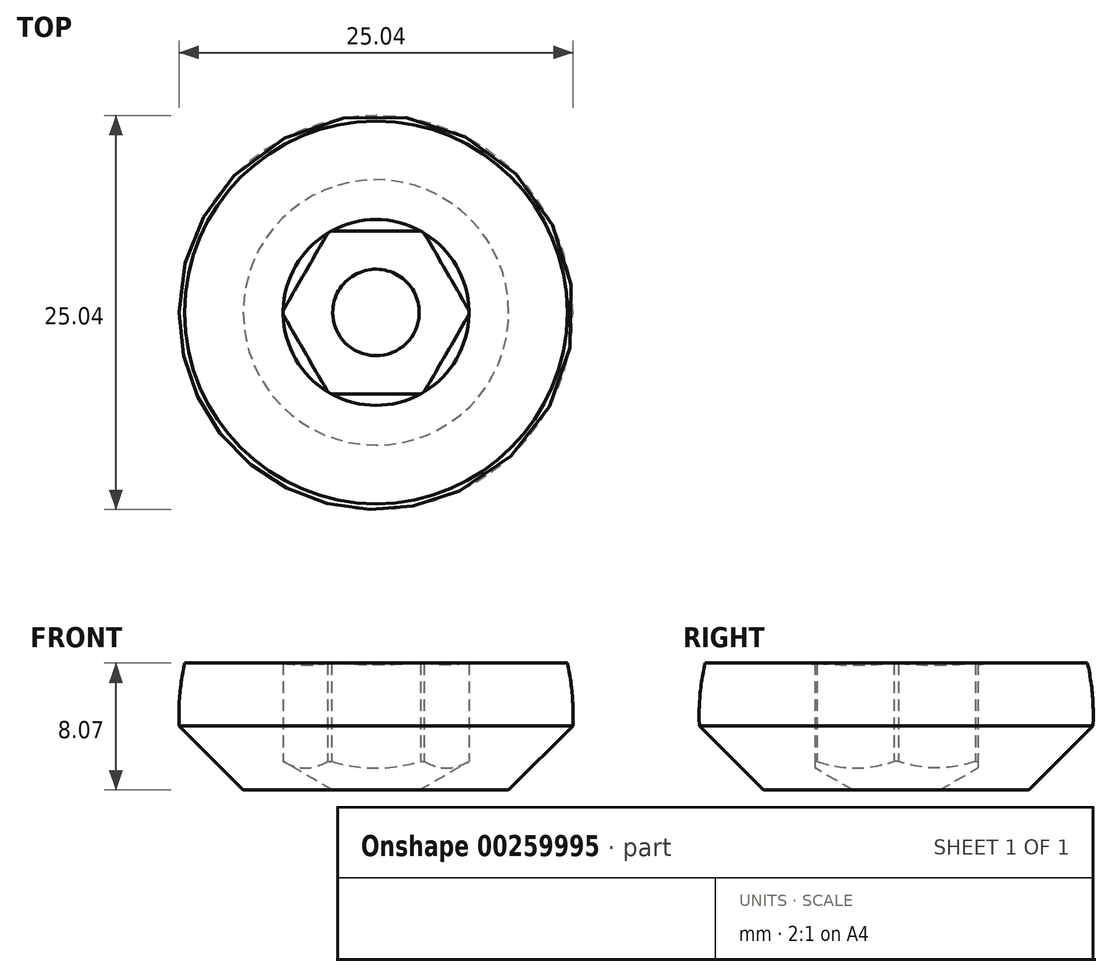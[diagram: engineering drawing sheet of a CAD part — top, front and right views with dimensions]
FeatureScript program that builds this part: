
annotation { "Feature Type Name" : "Feature", "Feature Type Description" : "" }
export const myFeature = defineFeature(function(context is Context, id is Id, definition is map)
    precondition{}
    {
        {
            var Q0;
            Q0=qCreatedBy(makeId("Front.planeOp"),FACE);
            var sketch = newSketch(context, id + "F0", { "sketchPlane" : qUnion([Q0])});
            skLineSegment(sketch, "E0", {"start": v(0, -0.86) * mm, "end": v(0, 0) * mm, "construction": true});
            skLineSegment(sketch, "E1", {"start": v(5.9, 8.07) * mm, "end": v(12.15, 8.07) * mm});
            skLineSegment(sketch, "E2", {"start": v(8.43, 0) * mm, "end": v(2.75, 0) * mm});
            skLineSegment(sketch, "E3", {"start": v(5.9, 8.07) * mm, "end": v(5.9, 1.82) * mm});
            skLineSegment(sketch, "E4", {"start": v(5.9, 1.82) * mm, "end": v(2.75, 0) * mm});
            skLineSegment(sketch, "E5", {"start": v(8.43, 0) * mm, "end": v(12.5, 4.07) * mm});
            skArc(sketch, "E6", {"start": v(12.5, 4.07) * mm, "mid": v(12.46, 6.08) * mm, "end": v(12.15, 8.07) * mm});
            skPoint(sketch, "E7.start.orphan", {"position": v(1.25, -0.86) * mm});
            skSolve(sketch);
        }
        {
            var Q0;
            Q0=qSketchRegion(id+"F0",true);
            var Q1;
            Q1=sQuery(id+"F0.wireOp",EDGE,"E0");
            revolve(context, id + "F1", {"entities" : qUnion([Q0]), "axis" : qUnion([Q1]), "revolveType" : RevolveType.FULL});
        }
        {
            var Q0;
            Q0=makeQuery(id+"F1.opRevolve","SWEPT_FACE",FACE,{"disambiguationData":[OSD([sQuery(id+"F0.wireOp",EDGE,"E1")])]});
            var sketch = newSketch(context, id + "F2", { "sketchPlane" : qUnion([Q0])});
            skCircle(sketch, "E8", {"center": v(0, 0) * mm, "radius": 6.78 * mm});
            skCircle(sketch, "E9.cCircle", {"center": v(0, 0) * mm, "radius": 5.17 * mm, "construction": true});
            skLineSegment(sketch, "E9.0", {"start": v(-2.99, 5.17) * mm, "end": v(2.99, 5.17) * mm});
            skLineSegment(sketch, "E9.1", {"start": v(2.99, 5.18) * mm, "end": v(5.98, 0) * mm});
            skLineSegment(sketch, "E9.2", {"start": v(5.98, 0) * mm, "end": v(2.99, -5.18) * mm});
            skLineSegment(sketch, "E9.3", {"start": v(2.99, -5.17) * mm, "end": v(-2.99, -5.17) * mm});
            skLineSegment(sketch, "E9.4", {"start": v(-2.99, -5.17) * mm, "end": v(-5.98, 0) * mm});
            skLineSegment(sketch, "E9.5", {"start": v(-5.98, 0) * mm, "end": v(-2.99, 5.17) * mm});
            skPoint(sketch, "E9.0.midPoint", {"position": v(0, 5.17) * mm});
            skSolve(sketch);
        }
        {
            var Q0;
            Q0=qSketchRegion(id+"F2",true);
            var Q1;
            Q1=makeQuery(id+"F1.opRevolve","SWEPT_FACE",FACE,{"disambiguationData":[OSD([sQuery(id+"F0.wireOp",EDGE,"E4")])]});
            extrude(context, id + "F3", {"entities" : qUnion([Q0]), "operationType" : NewBodyOperationType.ADD, "endBound" : BoundingType.UP_TO_SURFACE, "oppositeDirection" : true, "endBoundEntityFace" : qUnion([Q1]), "depth" : 25 * mm});
        }
        {
            var Q0;
            Q0=makeQuery(id+"F3.boolean.opBoolean","MERGE",FACE,{"derivedFrom":[makeQuery(id+"F1.opRevolve","SWEPT_FACE",FACE,{"disambiguationData":[OSD([sQuery(id+"F0.wireOp",EDGE,"E1")])]}),makeQuery(id+"F3.opExtrude","CAP_FACE",FACE,{"disambiguationData":[OSD([sQuery(id+"F2.wireOp",EDGE,"axiUSiGf-8ymJ-Ezfh-tHsk-ULXXzRlxOoBz"),sQuery(id+"F2.wireOp",EDGE,"WrdyBTnM-XU54-uk96-2Sjo-h1HHDxb1zyqn"),sQuery(id+"F2.wireOp",EDGE,"7iNK7enz-fUzD-7EQp-KRCh-aPKnPlRcPdaK"),sQuery(id+"F2.wireOp",EDGE,"e7c95674-c634-4135-8625-61586754ee6a.1.0"),sQuery(id+"F2.wireOp",EDGE,"e7c95674-c634-4135-8625-61586754ee6a.1.1"),sQuery(id+"F2.wireOp",EDGE,"e7c95674-c634-4135-8625-61586754ee6a.1.2"),sQuery(id+"F2.wireOp",EDGE,"e7c95674-c634-4135-8625-61586754ee6a.2.0"),sQuery(id+"F2.wireOp",EDGE,"e7c95674-c634-4135-8625-61586754ee6a.2.1"),sQuery(id+"F2.wireOp",EDGE,"e7c95674-c634-4135-8625-61586754ee6a.2.2"),sQuery(id+"F2.wireOp",EDGE,"e7c95674-c634-4135-8625-61586754ee6a.3.0"),sQuery(id+"F2.wireOp",EDGE,"e7c95674-c634-4135-8625-61586754ee6a.3.1"),sQuery(id+"F2.wireOp",EDGE,"e7c95674-c634-4135-8625-61586754ee6a.3.2"),sQuery(id+"F2.wireOp",EDGE,"e7c95674-c634-4135-8625-61586754ee6a.4.0"),sQuery(id+"F2.wireOp",EDGE,"e7c95674-c634-4135-8625-61586754ee6a.4.1"),sQuery(id+"F2.wireOp",EDGE,"e7c95674-c634-4135-8625-61586754ee6a.4.2"),sQuery(id+"F2.wireOp",EDGE,"e7c95674-c634-4135-8625-61586754ee6a.5.0"),sQuery(id+"F2.wireOp",EDGE,"e7c95674-c634-4135-8625-61586754ee6a.5.1"),sQuery(id+"F2.wireOp",EDGE,"e7c95674-c634-4135-8625-61586754ee6a.5.2"),sQuery(id+"F2.wireOp",EDGE,"c34f7dbc-1fd9-48ae-9599-0fb72b0d65de.filletArc"),sQuery(id+"F2.wireOp",EDGE,"5fecc0f4-c57f-42b8-a97f-f8fbf54cf4db.filletArc"),sQuery(id+"F2.wireOp",EDGE,"b077568f-b672-48a6-a184-fa18c1575088.filletArc"),sQuery(id+"F2.wireOp",EDGE,"4c4ba650-eb3b-40a6-a5b6-7d0bcd232093.filletArc"),sQuery(id+"F2.wireOp",EDGE,"b016cc09-0b8d-437b-9508-1d7630c9d4ff.filletArc"),sQuery(id+"F2.wireOp",EDGE,"d5479cb3-145b-41e2-b586-5ab3f6452500.filletArc"),sQuery(id+"F2.wireOp",EDGE,"E8")])],"isStart":true})]});
            var sketch = newSketch(context, id + "F4", { "sketchPlane" : qUnion([Q0])});
            skCircle(sketch, "E10", {"center": v(0, 0) * mm, "radius": 5.9 * mm});
            skSolve(sketch);
        }
        {
            var Q0;
            Q0=qSketchRegion(id+"F4",true);
            extrude(context, id + "F5", {"entities" : qUnion([Q0]), "operationType" : NewBodyOperationType.REMOVE, "oppositeDirection" : true, "offsetDistance" : 25 * mm, "depth" : 1 * mm, "hasDraft" : true, "draftAngle" : 80 * degree, "draftPullDirection" : true});
        }
    });
